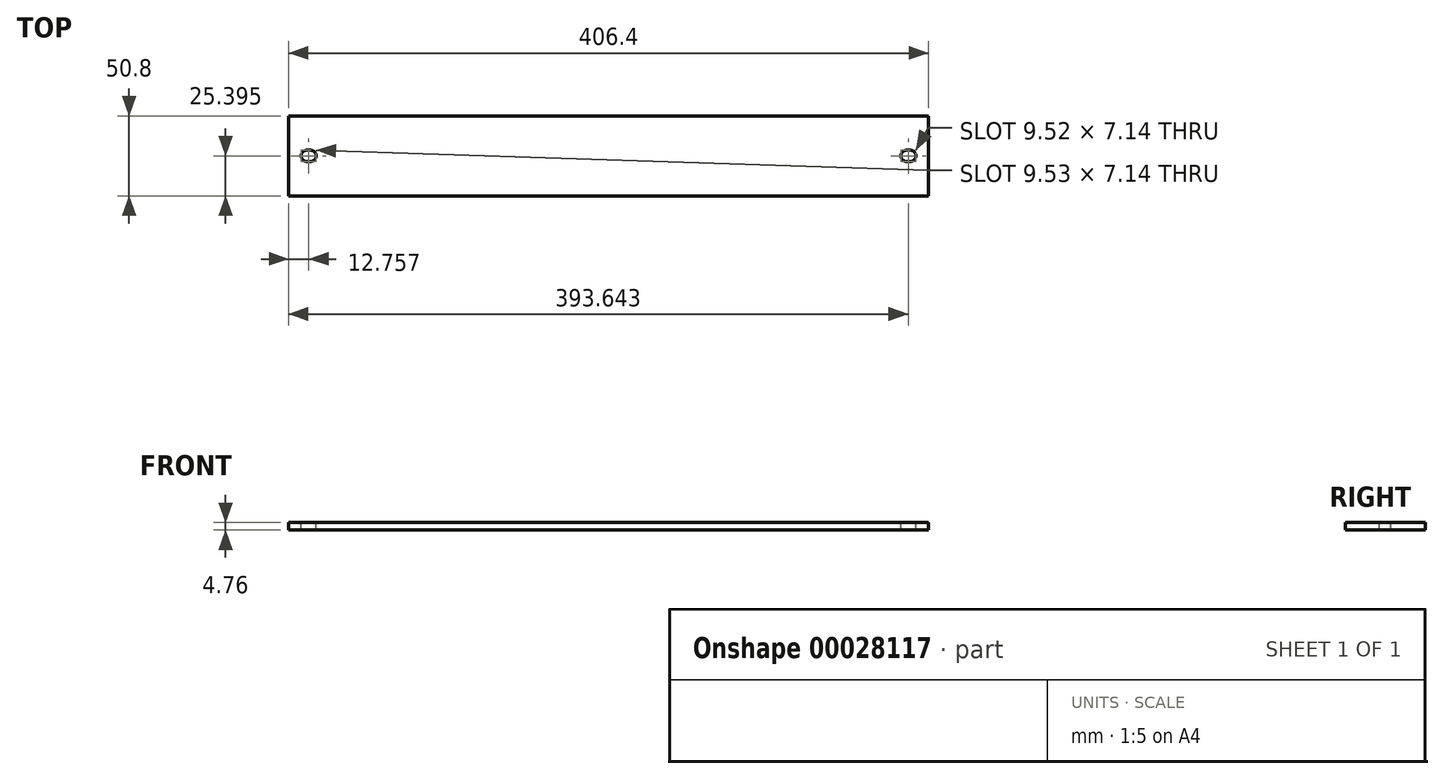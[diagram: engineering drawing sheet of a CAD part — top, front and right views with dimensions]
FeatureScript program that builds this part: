
annotation { "Feature Type Name" : "Feature", "Feature Type Description" : "" }
export const myFeature = defineFeature(function(context is Context, id is Id, definition is map)
    precondition{}
    {
        {
            var Q0;
            Q0=qCreatedBy(makeId("Top.planeOp"),FACE);
            var sketch = newSketch(context, id + "F0", { "sketchPlane" : qUnion([Q0])});
            skLineSegment(sketch, "E0.bottom", {"start": v(-200.83, -69) * mm, "end": v(205.57, -69) * mm});
            skLineSegment(sketch, "E0.top", {"start": v(-200.83, -119.8) * mm, "end": v(205.57, -119.8) * mm});
            skLineSegment(sketch, "E0.left", {"start": v(-200.83, -69) * mm, "end": v(-200.83, -119.8) * mm});
            skLineSegment(sketch, "E0.right", {"start": v(205.57, -69) * mm, "end": v(205.57, -119.8) * mm});
            skSolve(sketch);
        }
        {
            var Q0;
            Q0 = qSketchRegion(id + "F0", true);
            extrude(context, id + "F1", {"entities" : qUnion([Q0]), "depth" : 4.76 * mm});
        }
        {
            var Q0;
            Q0=makeQuery(id+"F1.opExtrude","CAP_FACE",FACE,{"disambiguationData":[OSD([sQuery(id+"F0.wireOp",EDGE,"E0.bottom"),sQuery(id+"F0.wireOp",EDGE,"E0.top"),sQuery(id+"F0.wireOp",EDGE,"E0.left"),sQuery(id+"F0.wireOp",EDGE,"E0.right")])],"isStart":false});
            var sketch = newSketch(context, id + "F2", { "sketchPlane" : qUnion([Q0])});
            skArc(sketch, "E1", {"start": v(194, -97.97) * mm, "mid": v(197.58, -94.4) * mm, "end": v(194, -90.82) * mm});
            skArc(sketch, "E2", {"start": v(191.62, -90.82) * mm, "mid": v(188.05, -94.4) * mm, "end": v(191.62, -97.97) * mm});
            skLineSegment(sketch, "E3", {"start": v(191.62, -97.97) * mm, "end": v(194, -97.97) * mm});
            skLineSegment(sketch, "E4", {"start": v(194, -90.82) * mm, "end": v(191.62, -90.82) * mm});
            skLineSegment(sketch, "E5", {"start": v(2.37, -69) * mm, "end": v(2.37, -119.8) * mm, "construction": true});
            skLineSegment(sketch, "E6.MirrorCS", {"start": v(-186.88, -97.97) * mm, "end": v(-189.26, -97.97) * mm});
            skArc(sketch, "E7.MirrorCS", {"start": v(-189.26, -97.97) * mm, "mid": v(-192.84, -94.4) * mm, "end": v(-189.26, -90.82) * mm});
            skLineSegment(sketch, "E8.MirrorCS", {"start": v(-189.26, -90.82) * mm, "end": v(-186.88, -90.82) * mm});
            skArc(sketch, "E9.MirrorCS", {"start": v(-186.88, -90.82) * mm, "mid": v(-183.31, -94.4) * mm, "end": v(-186.88, -97.97) * mm});
            skSolve(sketch);
        }
        {
            var Q0;
            Q0 = qSketchRegion(id + "F2", true);
            extrude(context, id + "F3", {"entities" : qUnion([Q0]), "operationType" : NewBodyOperationType.REMOVE, "endBound" : BoundingType.THROUGH_ALL, "oppositeDirection" : true, "depth" : 25.4 * mm});
        }
    });
